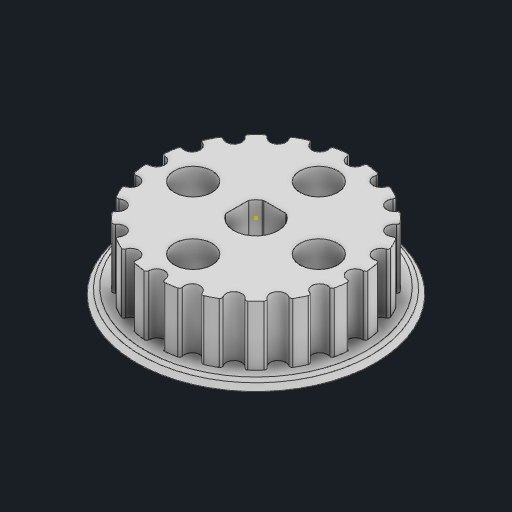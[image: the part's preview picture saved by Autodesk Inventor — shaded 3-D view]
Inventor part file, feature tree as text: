
AUTODESK INVENTOR PART (.ipt)
format: ipt  version: 2024 (Build 280153000, 153)  size: 283,136 bytes
history: native  units: in
note: dims shown in document units (in); Inventor stores cm internally (conversion verified against a paired STEP export)
features: sketch x5, other x3
ambient origin geometry x8: Origin, YZ Plane, XZ Plane, XY Plane, X Axis, Y Axis, Z Axis, Center Point
bodies: Solid1 (feature_tree)
feature tree (8):
  other  "MuftaForRemenSmall.ipt"
  other  "Solid1::MuftaForRemenSmall.ipt"
  other  "TaggingFeature1"
  sketch  "Sketch1"  dims[d0=0.3937in]
  sketch  "Sketch2"
  sketch  "Sketch3"
  sketch  "Sketch4"
  sketch  "Sketch5"
